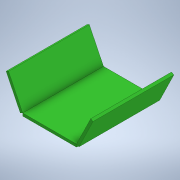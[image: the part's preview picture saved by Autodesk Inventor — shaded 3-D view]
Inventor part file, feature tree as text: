
AUTODESK INVENTOR PART (.ipt)
format: ipt  version: 2020 (Build 240168000, 168)  size: 115,712 bytes
history: native  units: mm
features: extrude x1, sketch x1
ambient origin geometry x8: Origin, YZ Plane, XZ Plane, XY Plane, X Axis, Y Axis, Z Axis, Center Point
bodies: Solid1 (feature_tree)
feature tree (2):
  extrude  "Extrusion1"  Depth=1.0mm
  sketch  "Sketch1"  dims[d0=20.0mm d1=1.0mm d2=1.0mm d3=1.0mm d4=32.0mm d5=12.0mm d6=12.0mm d7=30.0mm d8=0.0mm]
